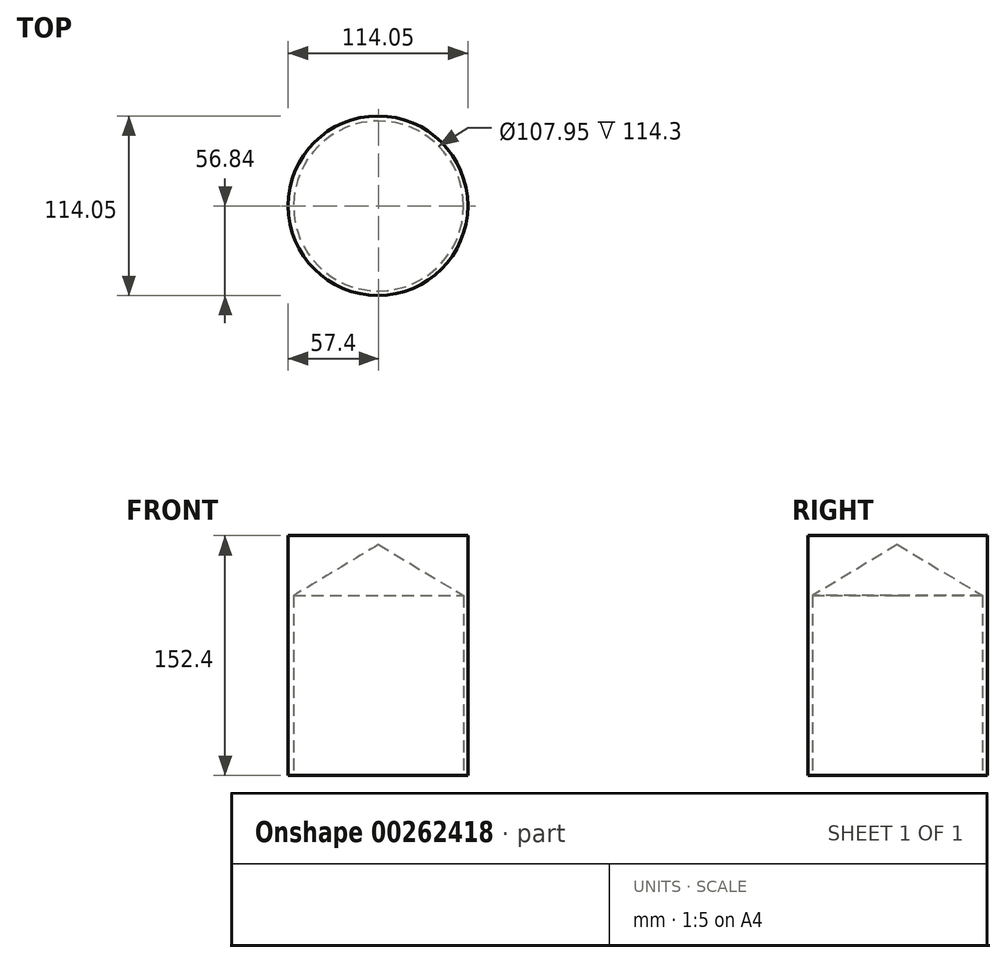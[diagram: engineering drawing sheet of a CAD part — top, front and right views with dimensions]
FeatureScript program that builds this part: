
annotation { "Feature Type Name" : "Feature", "Feature Type Description" : "" }
export const myFeature = defineFeature(function(context is Context, id is Id, definition is map)
    precondition{}
    {
        {
            var Q0;
            Q0=qCreatedBy(makeId("Top.planeOp"),FACE);
            var sketch = newSketch(context, id + "F0", { "sketchPlane" : qUnion([Q0])});
            skCircle(sketch, "E0", {"center": v(-0.38, 0.19) * mm, "radius": 57.03 * mm});
            skSolve(sketch);
        }
        {
            var Q0;
            Q0=makeQuery(id+"F0.imprint","IMPRINT",FACE,{"disambiguationData":[TD([[makeQuery(id+"F0.imprint","IMPRINT",EDGE,{"derivedFrom":sQuery(id+"F0.wireOp",EDGE,"E0")}),1.0]])]});
            extrude(context, id + "F1", {"entities" : qUnion([Q0]), "depth" : 152.4 * mm});
        }
        {
            var Q0;
            Q0=qCreatedBy(makeId("Top.planeOp"),FACE);
            var sketch = newSketch(context, id + "F2", { "sketchPlane" : qUnion([Q0])});
            skLineSegment(sketch, "E1.bottom", {"start": v(0, 0) * mm, "end": v(29.35, 0) * mm});
            skLineSegment(sketch, "E1.top", {"start": v(0, 23.33) * mm, "end": v(29.35, 23.33) * mm});
            skLineSegment(sketch, "E1.left", {"start": v(0, 0) * mm, "end": v(0, 23.33) * mm});
            skLineSegment(sketch, "E1.right", {"start": v(29.35, 0) * mm, "end": v(29.35, 23.33) * mm});
            skSolve(sketch);
        }
        {
            var Q0;
            Q0=sQuery(id+"F2.wireOp",VERTEX,"E1.left.start");
            var Q1;
            Q1=makeQuery(id+"F1.opExtrude","SWEPT_BODY",BODY,{"disambiguationData":[OSD([sQuery(id+"F0.wireOp",EDGE,"E0")])]});
            hole(context, id + "F3", {"style" : HoleStyle.SIMPLE, "endStyle" : HoleEndStyle.BLIND, "oppositeDirection" : true, "holeDiameter" : 107.95 * mm, "holeDepth" : 114.3 * mm, "tappedDepth" : 12.7 * mm, "tapClearance" : 3, "locations" : qUnion([Q0]), "scope" : qUnion([Q1])});
        }
    });
